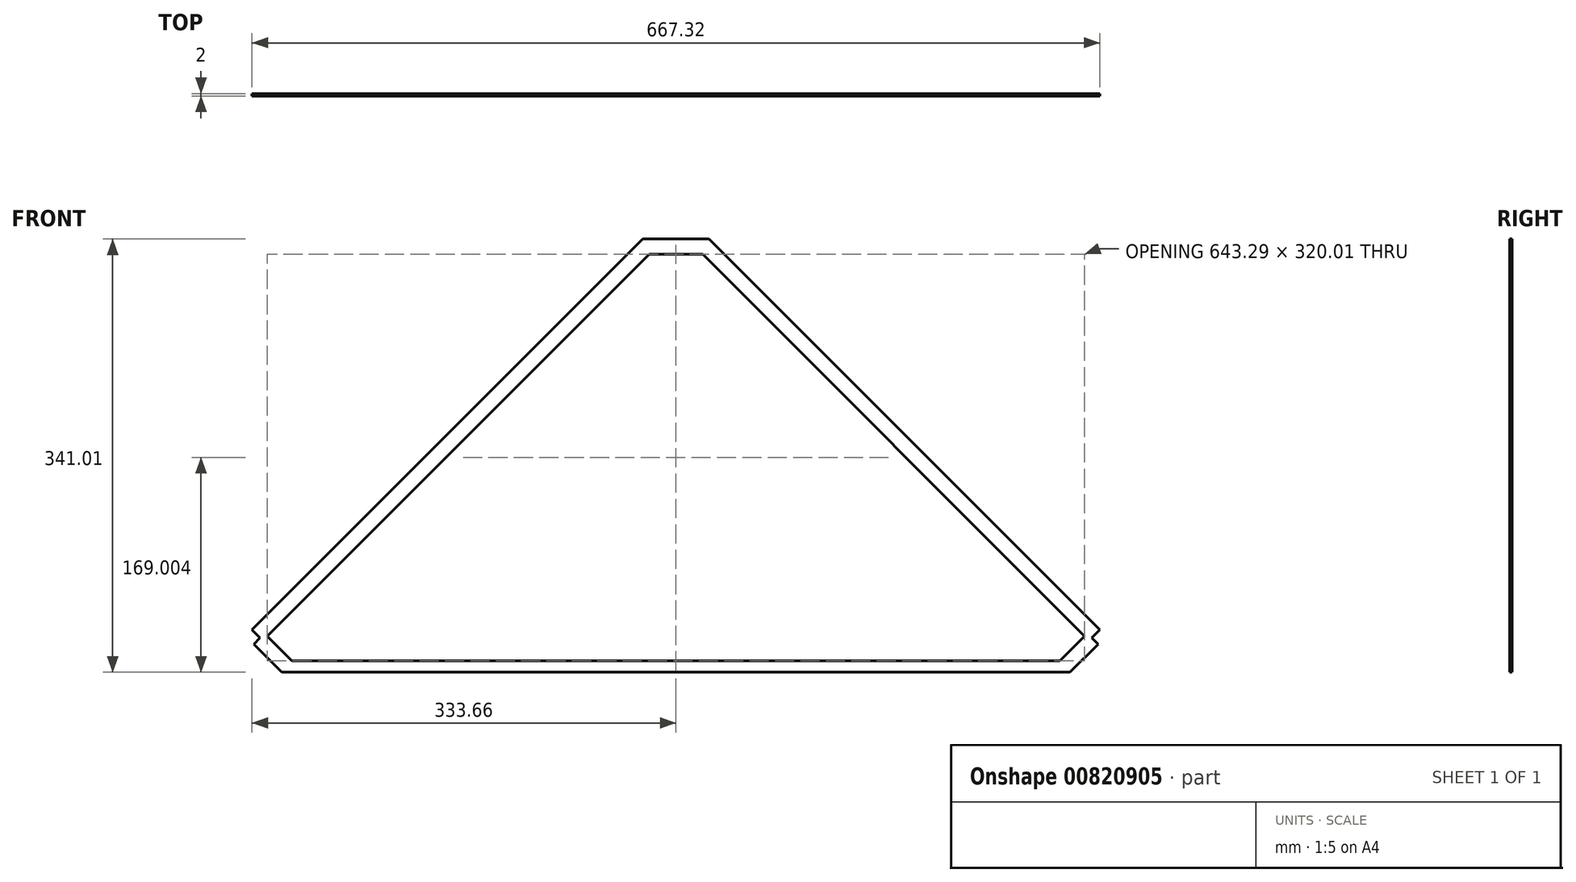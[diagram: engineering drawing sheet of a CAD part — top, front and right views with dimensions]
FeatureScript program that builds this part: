
annotation { "Feature Type Name" : "Feature", "Feature Type Description" : "" }
export const myFeature = defineFeature(function(context is Context, id is Id, definition is map)
    precondition{}
    {
        {
            var Q0;
            Q0=qCreatedBy(makeId("Front.planeOp"),FACE);
            var sketch = newSketch(context, id + "F0", { "sketchPlane" : qUnion([Q0])});
            skLineSegment(sketch, "E0", {"start": v(333.66, 36.42) * mm, "end": v(26.07, 344) * mm});
            skLineSegment(sketch, "E1", {"start": v(333.66, 36.42) * mm, "end": v(327.3, 30.05) * mm});
            skLineSegment(sketch, "E2", {"start": v(327.3, 30.05) * mm, "end": v(332.25, 25.1) * mm});
            skLineSegment(sketch, "E3", {"start": v(332.25, 25.1) * mm, "end": v(307.15, 0) * mm});
            skPoint(sketch, "E4", {"position": v(333.66, 36.42) * mm});
            skPoint(sketch, "E5", {"position": v(307.15, 0) * mm});
            skLineSegment(sketch, "E6", {"start": v(0, 427.88) * mm, "end": v(0, -107.1) * mm, "construction": true});
            skPoint(sketch, "E7", {"position": v(0, 0) * mm});
            skPoint(sketch, "E8.orphan", {"position": v(-392.17, 0) * mm});
            skPoint(sketch, "E9", {"position": v(26.07, 344) * mm});
            skLineSegment(sketch, "E10", {"start": v(26.07, 344) * mm, "end": v(0, 344) * mm});
            skPoint(sketch, "E11", {"position": v(0, 344) * mm});
            skLineSegment(sketch, "E12", {"start": v(307.15, 0) * mm, "end": v(0, 0) * mm});
            skLineSegment(sketch, "E13.MirrorCS", {"start": v(-26.07, 344) * mm, "end": v(0, 344) * mm});
            skLineSegment(sketch, "E14.MirrorCS", {"start": v(-333.66, 36.42) * mm, "end": v(-26.07, 344) * mm});
            skLineSegment(sketch, "E15.MirrorCS", {"start": v(-333.66, 36.42) * mm, "end": v(-327.3, 30.05) * mm});
            skLineSegment(sketch, "E16.MirrorCS", {"start": v(-327.3, 30.05) * mm, "end": v(-332.25, 25.1) * mm});
            skLineSegment(sketch, "E17.MirrorCS", {"start": v(-332.25, 25.1) * mm, "end": v(-307.15, 0) * mm});
            skLineSegment(sketch, "E18.MirrorCS", {"start": v(-307.15, 0) * mm, "end": v(0, 0) * mm});
            skSolve(sketch);
        }
        {
            var Q0;
            Q0 = qSketchRegion(id + "F0", true);
            extrude(context, id + "F1", {"entities" : qUnion([Q0]), "depth" : 2 * mm, "offsetDistance" : 25 * mm});
        }
        {
            var Q0;
            Q0=makeQuery(id+"F1.opExtrude","CAP_FACE",FACE,{"disambiguationData":[OSD([sQuery(id+"F0.wireOp",EDGE,"E0"),sQuery(id+"F0.wireOp",EDGE,"E1"),sQuery(id+"F0.wireOp",EDGE,"E2"),sQuery(id+"F0.wireOp",EDGE,"E3"),sQuery(id+"F0.wireOp",EDGE,"E10"),sQuery(id+"F0.wireOp",EDGE,"E12"),sQuery(id+"F0.wireOp",EDGE,"E13.MirrorCS"),sQuery(id+"F0.wireOp",EDGE,"E14.MirrorCS"),sQuery(id+"F0.wireOp",EDGE,"E15.MirrorCS"),sQuery(id+"F0.wireOp",EDGE,"E16.MirrorCS"),sQuery(id+"F0.wireOp",EDGE,"E17.MirrorCS"),sQuery(id+"F0.wireOp",EDGE,"E18.MirrorCS")])],"isStart":false});
            var sketch = newSketch(context, id + "F2", { "sketchPlane" : qUnion([Q0])});
            skLineSegment(sketch, "E19", {"start": v(0, 0) * mm, "end": v(0, 357.92) * mm, "construction": true});
            skLineSegment(sketch, "E20", {"start": v(21.1, 332) * mm, "end": v(0, 332) * mm});
            skLineSegment(sketch, "E21", {"start": v(302.18, 12) * mm, "end": v(0, 12) * mm});
            skLineSegment(sketch, "E22", {"start": v(302.18, 12) * mm, "end": v(321.64, 31.47) * mm});
            skLineSegment(sketch, "E23", {"start": v(21.1, 332) * mm, "end": v(321.64, 31.47) * mm});
            skPoint(sketch, "E24", {"position": v(321.64, 31.47) * mm});
            skLineSegment(sketch, "E25.MirrorCS", {"start": v(-21.1, 332) * mm, "end": v(0, 332) * mm});
            skLineSegment(sketch, "E26.MirrorCS", {"start": v(-21.1, 332) * mm, "end": v(-321.64, 31.47) * mm});
            skLineSegment(sketch, "E27.MirrorCS", {"start": v(-302.18, 12) * mm, "end": v(-321.64, 31.47) * mm});
            skLineSegment(sketch, "E28.MirrorCS", {"start": v(-302.18, 12) * mm, "end": v(0, 12) * mm});
            skSolve(sketch);
        }
        {
            var Q0;
            Q0 = qSketchRegion(id + "F2", true);
            extrude(context, id + "F3", {"entities" : qUnion([Q0]), "operationType" : NewBodyOperationType.REMOVE, "oppositeDirection" : true, "depth" : 2 * mm, "offsetDistance" : 25 * mm});
        }
        {
            var Q0;
            Q0=makeQuery(id+"F1.opExtrude","CAP_FACE",FACE,{"disambiguationData":[OSD([sQuery(id+"F0.wireOp",EDGE,"E0"),sQuery(id+"F0.wireOp",EDGE,"E1"),sQuery(id+"F0.wireOp",EDGE,"E2"),sQuery(id+"F0.wireOp",EDGE,"E3"),sQuery(id+"F0.wireOp",EDGE,"E10"),sQuery(id+"F0.wireOp",EDGE,"E12"),sQuery(id+"F0.wireOp",EDGE,"E13.MirrorCS"),sQuery(id+"F0.wireOp",EDGE,"E14.MirrorCS"),sQuery(id+"F0.wireOp",EDGE,"E15.MirrorCS"),sQuery(id+"F0.wireOp",EDGE,"E16.MirrorCS"),sQuery(id+"F0.wireOp",EDGE,"E17.MirrorCS"),sQuery(id+"F0.wireOp",EDGE,"E18.MirrorCS")])],"isStart":false});
            var sketch = newSketch(context, id + "F4", { "sketchPlane" : qUnion([Q0])});
            skLineSegment(sketch, "E29.bottom", {"start": v(-325, 3) * mm, "end": v(325, 3) * mm});
            skLineSegment(sketch, "E29.top", {"start": v(-325, -3) * mm, "end": v(325, -3) * mm});
            skLineSegment(sketch, "E29.left", {"start": v(-325, 3) * mm, "end": v(-325, -3) * mm});
            skLineSegment(sketch, "E29.right", {"start": v(325, 3) * mm, "end": v(325, -3) * mm});
            skPoint(sketch, "E29.middle", {"position": v(0, 0) * mm});
            skSolve(sketch);
        }
        {
            var Q0;
            Q0 = qSketchRegion(id + "F4", true);
            extrude(context, id + "F5", {"entities" : qUnion([Q0]), "operationType" : NewBodyOperationType.REMOVE, "oppositeDirection" : true, "depth" : 2 * mm, "offsetDistance" : 25 * mm});
        }
    });
